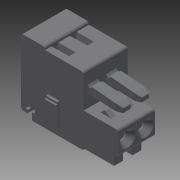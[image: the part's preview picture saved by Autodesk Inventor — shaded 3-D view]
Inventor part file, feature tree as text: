
AUTODESK INVENTOR PART (.ipt)
format: ipt  version: 2013 (Build 170138000, 138)  size: 346,112 bytes
history: native  units: mm
features: sketch x20, extrude x19, pattern_linear x6, revolve x1
ambient origin geometry x8: Origin, YZ Plane, XZ Plane, XY Plane, X Axis, Y Axis, Z Axis, Center Point
bodies: Solid1 (feature_tree)
feature tree (46):
  extrude  "Extrusion1"  Depth=1.5mm TaperAngle=0.0deg
  extrude  "Extrusion2"  Depth=1.5mm TaperAngle=0.0deg
  extrude  "Extrusion3"  Depth=1.5mm TaperAngle=0.0deg
  extrude  "Extrusion4"  Depth=1.5mm TaperAngle=0.0deg
  extrude  "Extrusion5"  TaperAngle=360.0deg  [1 undecoded]
  extrude  "Extrusion6"  Depth=3.3mm TaperAngle=0.0deg
  extrude  "Extrusion7"  Depth=1.0mm TaperAngle=0.0deg
  extrude  "Extrusion8"  Depth=1.0mm TaperAngle=0.0deg
  extrude  "Extrusion9"  Depth=0.9mm TaperAngle=0.0deg
  revolve  "Revolution1"  [1 undecoded]
  pattern_linear  "Rectangular Pattern1"  Count1=2 Spacing1=3.5mm
  extrude  "Extrusion10"  Depth=20.0mm TaperAngle=0.0deg
  pattern_linear  "Rectangular Pattern2"  [2 undecoded]
  extrude  "Extrusion11"  [1 undecoded]
  pattern_linear  "Rectangular Pattern3"  [2 undecoded]
  extrude  "Extrusion12"  [1 undecoded]
  pattern_linear  "Rectangular Pattern4"  [2 undecoded]
  extrude  "Extrusion13"  [1 undecoded]
  extrude  "Extrusion14"  [1 undecoded]
  extrude  "Extrusion15"  [1 undecoded]
  extrude  "Extrusion16"  [1 undecoded]
  extrude  "Extrusion17"  [1 undecoded]
  pattern_linear  "Rectangular Pattern5"  [2 undecoded]
  extrude  "Extrusion18"  [1 undecoded]
  pattern_linear  "Rectangular Pattern6"  [2 undecoded]
  extrude  "Extrusion19"  [1 undecoded]
  sketch  "Skizze_1"  dims[d0=7.0mm d1=0.0mm d2=1.5mm d3=0.0mm]
  sketch  "Skizze_3"  dims[d8=1.5mm d9=0.0mm d10=1.5mm d11=0.0mm]
  sketch  "Skizze_4"  dims[d12=1.5mm d13=0.0mm d14=1.5mm d15=0.0mm]
  sketch  "Skizze_5"  dims[d16=1.4mm d17=0.0mm d18=360.0deg]
  sketch  "Skizze_6"  dims[d19=20.0mm d21=3.5mm d22=10.0mm d24=0.0mm d25=3.3mm d26=0.0mm]
  sketch  "Skizze_7"  dims[d27=20.0mm d29=3.5mm d30=10.0mm d32=0.0mm d33=1.0mm d34=0.0mm]
  sketch  "Skizze_8"  dims[d35=20.0mm d37=3.5mm d38=10.0mm d40=0.0mm d41=1.0mm d42=0.0mm]
  sketch  "Skizze_9"  dims[d43=20.0mm d45=3.5mm d46=10.0mm d48=0.0mm d49=0.9mm d50=0.0mm]
  sketch  "Skizze_2"  dims[d4=1.5mm d5=0.0mm d6=1.5mm d7=0.0mm]
  sketch  "Skizze_10"  dims[d51=0.9mm d52=0.0mm d53=1.7mm d54=0.0mm]
  sketch  "Skizze_12"  dims[d55=1.7mm d56=0.0mm]
  sketch  "Skizze_14"  dims[d57=2.0mm d58=0.0mm d59=20.0mm d61=3.5mm d62=10.0mm d64=0.0mm]
  sketch  "Skizze_16"  dims[d65=1.7mm d66=0.0mm d67=20.0mm d69=3.5mm d70=10.0mm d72=0.0mm]
  sketch  "Skizze_18"  dims[d73=2.2mm d74=0.0mm]
  sketch  "Skizze_19"
  sketch  "Skizze_20"
  sketch  "Skizze_21"
  sketch  "Skizze_22"
  sketch  "Skizze_24"
  sketch  "Skizze_26"
note: 21 required parameter values undecoded (feature->parameter linkage not recoverable at this tier; creation-order binding heuristic only, values carry confidence <= 0.55)